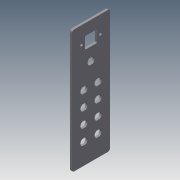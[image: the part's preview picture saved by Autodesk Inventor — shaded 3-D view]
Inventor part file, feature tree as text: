
AUTODESK INVENTOR PART (.ipt)
format: ipt  version: 2015 SP1 (Build 190203100, 203)  size: 229,888 bytes
history: native  units: mm
features: extrude x4, sketch x4, fillet x2, hole x1, projected_geometry x1
ambient origin geometry x8: Origin, YZ Plane, XZ Plane, XY Plane, X Axis, Y Axis, Z Axis, Center Point
bodies: Solid1 (feature_tree)
feature tree (12):
  extrude  "Extrusion1"  Depth=51.0mm
  fillet  "Fillet1"  Radius=3.0mm
  extrude  "Extrusion2"  Depth=3.0mm
  sketch  "Sketch4"  dims[d6=45.0mm d9=165.0mm d10=8.0mm]
  extrude  "Extrusion3"  Depth=165.0mm
  fillet  "Fillet2"  Radius=8.0mm
  hole  "Hole4"  [1 undecoded]
  extrude  "Extrusion4"  Depth=1.0mm TaperAngle=0.0deg
  sketch  "Sketch1"  dims[d0=165.0mm d1=51.0mm d2=3.0mm d3=0.0mm]
  sketch  "Sketch2"  dims[d4=3.0mm d5=149.0mm]
  sketch  "Sketch9"  dims[d11=51.0mm d12=3.0mm d13=0.1mm d14=0.0mm d16=20.0mm d17=20.0mm d18=20.0mm d20=19.0mm d25=20.0mm d26=20.0mm d27=20.0mm d28=19.0mm d29=19.0mm d43=13.0mm d44=45.0mm d45=13.0mm d46=13.0mm d47=13.0mm d70=22.5mm d71=8.3mm d72=4.75mm d73=40.0mm d74=20.189156mm d75=8.3mm d76=4.75mm d77=8.3mm d78=4.75mm d79=8.3mm d81=8.3mm d82=8.3mm d83=8.3mm d84=8.3mm d85=4.75mm d86=4.75mm d88=4.75mm d90=4.75mm d98=20.0mm d100=20.0mm d101=8.3mm d102=20.0mm d103=0.0mm d104=16.0mm d105=16.0mm d106=15.0mm d107=22.5mm d108=8.0mm d109=8.0mm d110=12.7mm d111=12.7mm d119=1.0mm d120=3.4mm d121=5.69mm d122=3.023mm d123=2.0mm d124=14.3117mm d125=8.865mm d126=20.594885mm d127=0.1mm d128=0.0mm]
  projected_geometry  "Projected Loop1"
note: 1 required parameter value undecoded (feature->parameter linkage not recoverable at this tier; creation-order binding heuristic only, values carry confidence <= 0.55)
